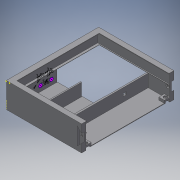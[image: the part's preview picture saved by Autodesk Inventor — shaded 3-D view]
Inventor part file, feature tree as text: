
AUTODESK INVENTOR PART (.ipt)
format: ipt  version: 2016 SP2 (Build 200236200, 236)  size: 1,026,560 bytes
history: native  units: mm
features: sketch x29, extrude x23, chamfer x14, projected_geometry x10, thread x2, revolve x2, other x2
ambient origin geometry x8: Origin, YZ Plane, XZ Plane, XY Plane, X Axis, Y Axis, Z Axis, Center Point
bodies: Volumenkörper1 (feature_tree), Volumenkörper2 (feature_tree), Volumenkörper3 (feature_tree)
feature tree (82):
  extrude  "Extrusion1"  Depth=9.0mm
  extrude  "Extrusion2"  Depth=10.0mm
  extrude  "Extrusion3"  Depth=1.0mm TaperAngle=0.0deg
  extrude  "Extrusion4"  Depth=1.5mm
  extrude  "Extrusion5"  Depth=17.0mm TaperAngle=0.0deg
  sketch  "Skizze6"  dims[d16=3.0mm d17=0.0mm d24=43.5mm]
  chamfer  "Fase2"  Distance=2.0mm
  chamfer  "Fase3"  Distance=23.0mm
  extrude  "Extrusion7"  Depth=43.5mm
  extrude  "Extrusion8"  Depth=2.0mm
  extrude  "Extrusion9"  Depth=1.5mm TaperAngle=45.0deg
  extrude  "Extrusion10"  Depth=78.5mm TaperAngle=0.0deg
  extrude  "Extrusion11"  Depth=82.5mm TaperAngle=0.0deg
  extrude  "Extrusion12"  Depth=2.0mm
  extrude  "Extrusion13"  Depth=1.0mm
  extrude  "Extrusion14"  Depth=2.0mm
  chamfer  "Fase4"  Distance=89.5mm
  chamfer  "Fase5"  Distance=4.5mm
  chamfer  "Fase6"  Distance=4.5mm
  chamfer  "Fase7"  Distance=2.0mm
  chamfer  "Fase9"  Distance=2.0mm
  chamfer  "Fase20"  Distance=2.0mm
  extrude  "Extrusion15"  Depth=2.0mm
  extrude  "Extrusion16"  Depth=5.0mm
  extrude  "Extrusion17"  Depth=5.0mm
  extrude  "Extrusion18"  Depth=40.0mm TaperAngle=0.0deg
  chamfer  "Fase14"  Distance=4.5mm
  chamfer  "Fase15"  Distance=18.0mm
  chamfer  "Fase16"  Distance=2.0mm
  chamfer  "Fase17"  Distance=2.0mm
  chamfer  "Fase18"  Distance=2.0mm
  chamfer  "Fase19"  Distance=2.0mm
  extrude  "Extrusion20"  Depth=10.0mm
  extrude  "Extrusion21"  Depth=10.0mm
  extrude  "Extrusion22"  Depth=10.0mm
  extrude  "Extrusion23"  Depth=10.0mm
  extrude  "Extrusion24"  Depth=10.0mm TaperAngle=0.0deg
  sketch  "Skizze26"  dims[d66=3.5mm d67=4.5mm d68=0.0mm]
  sketch  "Skizze27"  dims[d69=5.6mm d70=2.0mm d71=0.0mm d72=2.0mm d73=2.0mm d74=0.872665mm d75=2.0mm d76=2.0mm d77=0.872665mm]
  extrude  "Extrusion27"  Depth=10.0mm
  thread  "Gewinde1"  [1 undecoded]
  thread  "Gewinde2"  [1 undecoded]
  revolve  "Umdrehung1"
  other  "Spirale1"
  revolve  "Umdrehung2"
  other  "Spirale2"
  sketch  "Skizze1"  dims[d0=9.0mm d1=9.0mm]
  sketch  "Skizze2"  dims[d2=150.5mm d3=10.0mm]
  sketch  "Skizze3"  dims[d4=137.4mm d5=1.0mm d6=0.0mm]
  projected_geometry  "Projizierte Kontur1"
  sketch  "Skizze4"  dims[d7=1.5mm d8=1.5mm]
  projected_geometry  "Projizierte Kontur2"
  projected_geometry  "Projizierte Kontur3"
  projected_geometry  "Projizierte Kontur4"
  sketch  "Skizze5"  dims[d9=4.0mm d10=17.0mm d11=0.0mm d12=2.0mm d13=0.0mm d14=23.0mm d15=0.0mm]
  sketch  "Skizze7"  dims[d25=43.5mm d26=2.0mm]
  sketch  "Skizze8"  dims[d27=3.0mm d33=1.5mm d34=2.0mm d35=45.0deg]
  sketch  "Skizze9"  dims[d36=1.5mm d37=2.0mm d38=45.0deg d39=78.5mm d40=0.0mm]
  sketch  "Skizze10"  dims[d42=23.0mm d43=0.0mm d44=82.5mm d45=0.0mm]
  sketch  "Skizze11"  dims[d46=2.5mm d47=2.0mm]
  sketch  "Skizze13"  dims[d48=1.0mm d49=1.0mm]
  projected_geometry  "Projizierte Kontur5"
  sketch  "Skizze14"  dims[d50=89.5mm d51=0.0mm d52=2.0mm]
  sketch  "Skizze15"  dims[d53=1.0mm]
  sketch  "Skizze16"  dims[d54=2.0mm]
  projected_geometry  "Projizierte Kontur6"
  sketch  "Skizze17"  dims[d55=1.0mm d56=89.5mm d57=0.0mm]
  projected_geometry  "Projizierte Kontur7"
  sketch  "Skizze19"  dims[d58=15.0mm]
  projected_geometry  "Projizierte Kontur8"
  sketch  "Skizze21"  dims[d59=15.0mm]
  sketch  "Skizze22"  dims[d60=8.0mm]
  sketch  "Skizze23"  dims[d61=8.0mm]
  sketch  "Skizze24"  dims[d62=8.0mm]
  projected_geometry  "Projizierte Kontur9"
  projected_geometry  "Projizierte Kontur10"
  sketch  "Skizze25"  dims[d63=16.0mm d64=4.5mm d65=0.0mm]
  sketch  "Skizze28"  dims[d78=2.0mm d79=2.0mm d80=0.872665mm d81=2.0mm d82=2.0mm d83=0.872665mm]
  sketch  "Skizze29"  dims[d87=2.0mm d88=2.0mm d89=0.872665mm d90=5.0mm]
  sketch  "Skizze30"  dims[d91=5.0mm d92=40.0mm]
  sketch  "Skizze31"  dims[d93=9.0mm d94=40.0mm d95=0.0mm d96=4.5mm d97=0.0mm d98=18.0mm d99=0.0mm d100=2.0mm d101=0.0mm d114=2.0mm d115=2.0mm d116=0.872665mm d117=2.0mm d118=2.0mm d119=0.872665mm d120=2.0mm d121=2.0mm d122=0.872665mm]
  sketch  "Skizze32"  dims[d123=2.0mm d124=2.0mm d125=0.872665mm d126=2.0mm d127=2.0mm d128=0.872665mm d129=2.0mm d130=2.0mm d131=0.872665mm d134=2.0mm d135=2.0mm d136=0.872665mm d137=8.0mm d138=2.0mm d139=0.0mm d140=10.0mm d141=10.0mm d142=10.0mm d143=10.0mm d144=5.0mm d145=0.0mm d146=8.0mm d147=8.0mm d148=8.0mm d149=8.0mm d150=2.5mm d151=0.0mm d152=3.5mm d153=3.5mm d154=4.5mm d155=0.0mm d156=5.8mm d157=5.8mm d158=2.5mm d159=0.0mm d160=3.5mm d161=3.5mm d162=10.0mm d163=20.0mm d166=5.8mm d167=5.8mm d170=10.0mm d171=10.0mm d172=10.0mm d173=25.0mm d174=5.0mm d175=0.0mm d176=10.0mm d177=0.0mm d178=10.0mm d179=0.0mm d180=60.0deg d181=0.240125mm d182=0.240125mm d185=1.5mm d187=60.0deg d189=0.0mm d190=1.5015mm d191=8.0mm d192=10.0mm d193=0.0mm d194=0.0mm d195=0.0mm d196=0.0mm d197=0.0mm d198=60.0deg d199=0.240125mm d200=0.240125mm d203=1.5mm d205=60.0deg d207=0.0mm d208=1.5015mm d209=8.0mm d210=10.0mm d211=0.0mm d212=0.0mm d213=0.0mm d214=0.0mm d215=0.0mm]
note: 2 required parameter values undecoded (feature->parameter linkage not recoverable at this tier; creation-order binding heuristic only, values carry confidence <= 0.55)
